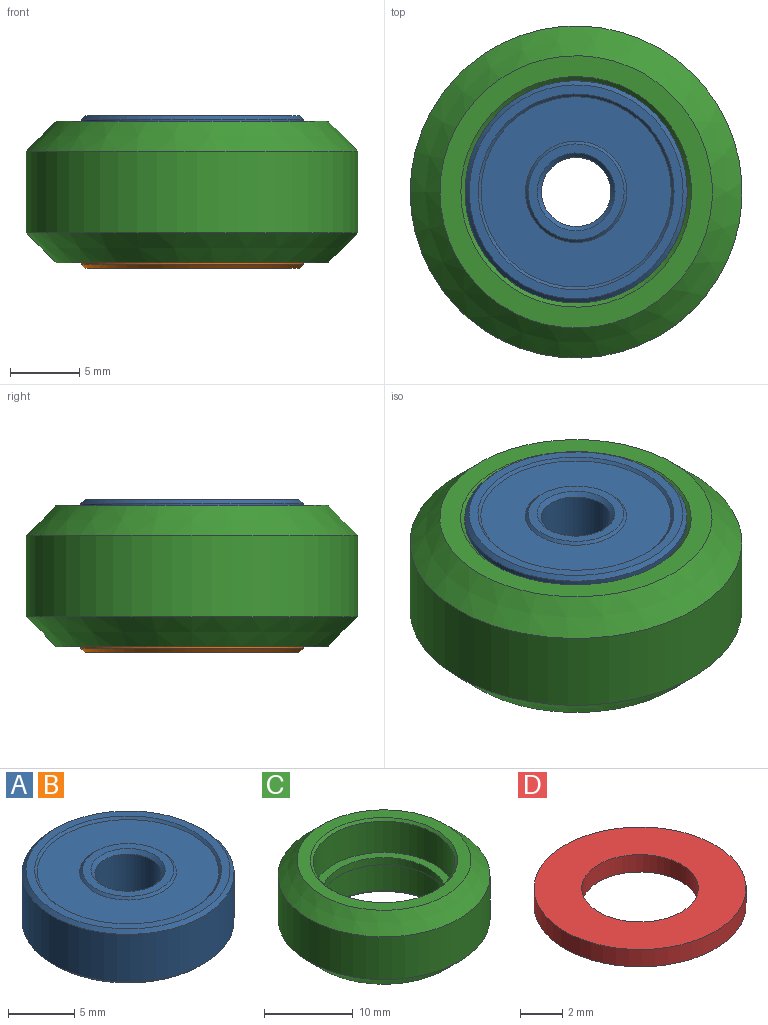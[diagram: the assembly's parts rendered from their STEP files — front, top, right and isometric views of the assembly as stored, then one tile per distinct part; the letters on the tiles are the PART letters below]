
ASSEMBLY  parts=4 mates=3
PART A: 16 faces, bbox 16x16x5 mm
  f0: plane 13.7x13.7mm, normal (0,0,1), area 105.6mm2, adj f13,f14
  f1: plane 13.7x13.7mm, normal (0,0,-1), area 105.6mm2, adj f9,f10
  f2: cylinder r=2.5mm len=5mm, axis (0,0,-1), area 69.1mm2, adj f8,f12
  f3: plane 6.9x6.9mm, normal (0,0,1), area 12.8mm2, adj f12,f13
  f4: plane 6.9x6.9mm, normal (0,0,-1), area 12.8mm2, adj f8,f9
  f5: cylinder r=8mm len=16mm, axis (0,0,-1), area 221.2mm2, adj f11,f15
  f6: plane 15.4x15.4mm, normal (0,0,1), area 30.1mm2, adj f14,f15
  f7: plane 15.4x15.4mm, normal (0,0,-1), area 30.1mm2, adj f10,f11
  f8: cone r=2.8mm half-angle=45deg, axis (0,0,-1), area 7.1mm2, adj f2,f4
  f9: cone r=3.75mm half-angle=45deg, axis (0,0,1), area 6.3mm2, adj f1,f4
  f10: cone r=7.05mm half-angle=45deg, axis (0,0,-1), area 12.4mm2, adj f1,f7
  f11: cone r=8mm half-angle=45deg, axis (0,0,1), area 20.9mm2, adj f5,f7
  f12: cone r=2.5mm half-angle=45deg, axis (0,0,1), area 7.1mm2, adj f2,f3
  f13: cone r=3.45mm half-angle=45deg, axis (0,0,-1), area 6.3mm2, adj f0,f3
  f14: cone r=6.75mm half-angle=45deg, axis (0,0,1), area 12.4mm2, adj f0,f6
  f15: cone r=7.7mm half-angle=45deg, axis (0,0,-1), area 20.9mm2, adj f5,f6
PART B: same geometry as A
PART C: 12 faces, bbox 23.9x23.9x10.2 mm
  f0: cylinder r=8mm len=16mm, axis (0,0,-1), area 216.1mm2, adj f1,f11
  f1: plane 16x16mm, normal (0,0,-1), area 47.1mm2, adj f0,f2
  f2: cylinder r=7mm len=14mm, axis (0,0,-1), area 44mm2, adj f1,f3
  f3: plane 16x16mm, normal (0,0,1), area 47.1mm2, adj f2,f4
  f4: cylinder r=8mm len=16mm, axis (0,0,-1), area 216.1mm2, adj f3,f5
  f5: cone r=8.3mm half-angle=45deg, axis (0,0,1), area 21.7mm2, adj f4,f6
  f6: plane 19.6x19.6mm, normal (0,0,1), area 85.3mm2, adj f5,f7
  f7: cone r=9.8mm half-angle=45deg, axis (0,0,-1), area 207.8mm2, adj f6,f8
  f8: cylinder r=11.95mm len=23.9mm, axis (0,0,-1), area 443mm2, adj f7,f9
  f9: cone r=11.95mm half-angle=45deg, axis (0,0,1), area 207.8mm2, adj f8,f10
  f10: plane 19.6x19.6mm, normal (0,0,-1), area 85.3mm2, adj f9,f11
  f11: cone r=8.3mm half-angle=45deg, axis (0,0,-1), area 21.7mm2, adj f0,f10
PART D: 4 faces, bbox 10x10x1 mm
  f0: cylinder r=2.75mm len=5.5mm, axis (0,0,-1), area 17.3mm2, adj f2,f3
  f1: cylinder r=5mm len=10mm, axis (0,0,-1), area 31.4mm2, adj f2,f3
  f2: plane 10x10mm, normal (0,0,1), area 54.8mm2, adj f0,f1
  f3: plane 10x10mm, normal (0,0,-1), area 54.8mm2, adj f0,f1
PLACE A t=(-54.47,-38.08,27.23)mm
PLACE B t=(-54.47,-38.08,21.23)mm
PLACE C t=(-54.47,-38.08,26.73)mm
PLACE D t=(-54.47,-38.08,26.23)mm
MATE fastened A.f2 <-> C.f0  axis (0,0,-1) through (-54.47,-38.08,27.23)mm
MATE fastened D.f0 <-> C.f0  axis (0,0,-1) through (-54.47,-38.08,26.73)mm
MATE fastened B.f2 <-> C.f0  axis (0,0,1) through (-54.47,-38.08,26.23)mm
